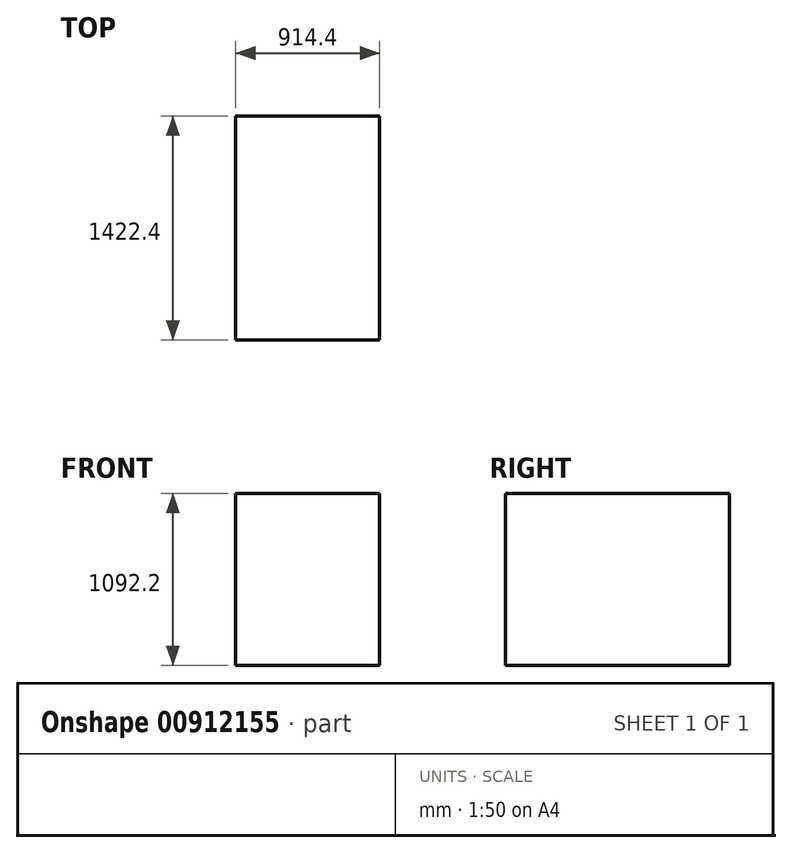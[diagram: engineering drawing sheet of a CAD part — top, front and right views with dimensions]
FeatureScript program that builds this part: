
annotation { "Feature Type Name" : "Feature", "Feature Type Description" : "" }
export const myFeature = defineFeature(function(context is Context, id is Id, definition is map)
    precondition{}
    {
        {
            var Q0;
            Q0=qCreatedBy(makeId("Front.planeOp"),FACE);
            var sketch = newSketch(context, id + "F0", { "sketchPlane" : qUnion([Q0])});
            skLineSegment(sketch, "E0.bottom", {"start": v(-876.87, 1063.87) * mm, "end": v(37.53, 1063.87) * mm});
            skLineSegment(sketch, "E0.top", {"start": v(-876.87, -28.33) * mm, "end": v(37.53, -28.33) * mm});
            skLineSegment(sketch, "E0.left", {"start": v(-876.87, 1063.87) * mm, "end": v(-876.87, -28.33) * mm});
            skLineSegment(sketch, "E0.right", {"start": v(37.53, 1063.87) * mm, "end": v(37.53, -28.33) * mm});
            skSolve(sketch);
        }
        {
            var Q0;
            Q0=makeQuery(id+"F0.imprint","IMPRINT",FACE,{"disambiguationData":[TD([[makeQuery(id+"F0.imprint","IMPRINT",EDGE,{"derivedFrom":sQuery(id+"F0.wireOp",EDGE,"E0.bottom")}),-1.0]])]});
            extrude(context, id + "F1", {"entities" : qUnion([Q0]), "oppositeDirection" : true, "depth" : 1422.4 * mm, "offsetDistance" : 25.4 * mm});
        }
    });
